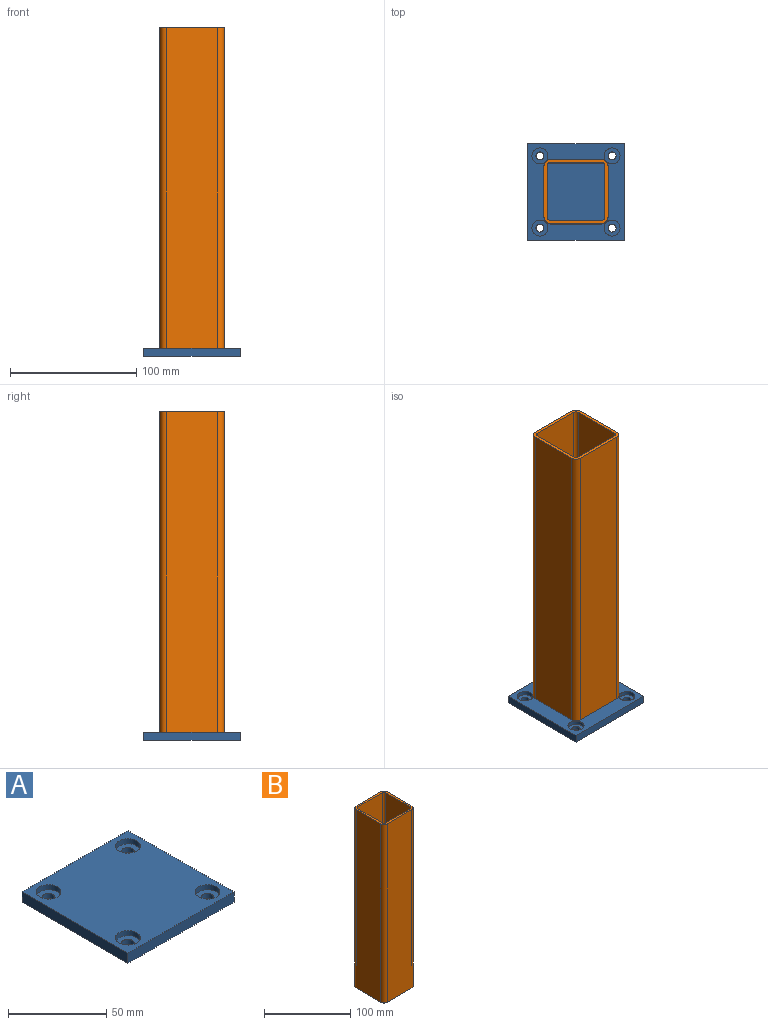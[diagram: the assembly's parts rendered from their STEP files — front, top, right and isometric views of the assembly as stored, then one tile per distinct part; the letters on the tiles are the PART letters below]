
ASSEMBLY  parts=2 mates=1
PART A: 18 faces, bbox 76.2x76.2x6.4 mm
  f0: plane 76.2x6.35mm, normal (0,1,0), area 483.9mm2, adj f1,f3,f4,f5
  f1: plane 76.2x6.35mm, normal (-1,0,0), area 483.9mm2, adj f0,f2,f4,f5
  f2: plane 76.2x6.35mm, normal (0,-1,0), area 483.9mm2, adj f1,f3,f4,f5
  f3: plane 76.2x6.35mm, normal (1,0,0), area 483.9mm2, adj f0,f2,f4,f5
  f4: plane 76.2x76.2mm, normal (0,0,1), area 5299.7mm2, adj f0,f1,f2,f3,f8,f11,f14,f17
  f5: plane 76.2x76.2mm, normal (0,0,-1), area 5679.8mm2, adj f0,f1,f2,f3,f6,f9,f12,f15
  f6: cylinder r=3.17mm len=6.35mm, axis (0,0,1), area 63.3mm2, adj f5,f7
  f7: plane 12.7x12.7mm, normal (0,0,1), area 95mm2, adj f6,f8
  f8: cylinder r=6.35mm len=12.7mm, axis (0,0,1), area 126.7mm2, adj f4,f7
  f9: cylinder r=3.17mm len=6.35mm, axis (0,0,1), area 63.3mm2, adj f5,f10
  f10: plane 12.7x12.7mm, normal (0,0,1), area 95mm2, adj f9,f11
  f11: cylinder r=6.35mm len=12.7mm, axis (0,0,1), area 126.7mm2, adj f4,f10
  f12: cylinder r=3.17mm len=6.35mm, axis (0,0,1), area 63.3mm2, adj f5,f13
  f13: plane 12.7x12.7mm, normal (0,0,1), area 95mm2, adj f12,f14
  f14: cylinder r=6.35mm len=12.7mm, axis (0,0,1), area 126.7mm2, adj f4,f13
  f15: cylinder r=3.17mm len=6.35mm, axis (0,0,1), area 63.3mm2, adj f5,f16
  f16: plane 12.7x12.7mm, normal (0,0,1), area 95mm2, adj f15,f17
  f17: cylinder r=6.35mm len=12.7mm, axis (0,0,1), area 126.7mm2, adj f4,f16
PART B: 18 faces, bbox 50.8x50.8x254 mm
  f0: plane 50.8x50.8mm, normal (0,0,1), area 473.7mm2, adj f2,f3,f4,f5,f6,f7,f8,f9
  f1: plane 50.8x50.8mm, normal (0,0,-1), area 473.7mm2, adj f2,f3,f4,f5,f6,f7,f8,f9
  f2: plane 254x40.64mm, normal (0,1,0), area 10322.6mm2, adj f0,f1,f6,f9
  f3: plane 254x40.64mm, normal (-1,0,0), area 10322.6mm2, adj f0,f1,f6,f7
  f4: plane 254x40.64mm, normal (0,-1,0), area 10322.6mm2, adj f0,f1,f7,f8
  f5: plane 254x40.64mm, normal (1,0,0), area 10322.6mm2, adj f0,f1,f8,f9
  f6: cylinder r=5.08mm len=254mm, axis (0,0,1), area 2026.8mm2, adj f0,f1,f2,f3
  f7: cylinder r=5.08mm len=254mm, axis (0,0,-1), area 2026.8mm2, adj f0,f1,f3,f4
  f8: cylinder r=5.08mm len=254mm, axis (0,0,1), area 2026.8mm2, adj f0,f1,f4,f5
  f9: cylinder r=5.08mm len=254mm, axis (0,0,-1), area 2026.8mm2, adj f0,f1,f2,f5
  f10: plane 254x40.64mm, normal (0,-1,0), area 10322.6mm2, adj f0,f1,f14,f17
  f11: plane 254x40.64mm, normal (1,0,0), area 10322.6mm2, adj f0,f1,f14,f15
  f12: plane 254x40.64mm, normal (0,1,0), area 10322.6mm2, adj f0,f1,f15,f16
  f13: plane 254x40.64mm, normal (-1,0,0), area 10322.6mm2, adj f0,f1,f16,f17
  f14: cylinder r=2.54mm len=254mm, axis (0,0,1), area 1013.4mm2, adj f0,f1,f10,f11
  f15: cylinder r=2.54mm len=254mm, axis (0,0,-1), area 1013.4mm2, adj f0,f1,f11,f12
  f16: cylinder r=2.54mm len=254mm, axis (0,0,1), area 1013.4mm2, adj f0,f1,f12,f13
  f17: cylinder r=2.54mm len=254mm, axis (0,0,-1), area 1013.4mm2, adj f0,f1,f10,f13
PLACE A t=(-50.8,0,47.24)mm
PLACE B t=(-50.8,0,53.59)mm
MATE fastened B.f1 <-> A.f4  axis (0,0,-1) through (-50.8,0,53.59)mm
